# Revit family: Backflow_Preventer-DCDA-Zurn_Wilkins-Model_450DABG-(8-10_Inch)
name_source: partatom
category: Pipe Accessories
units: mm (PartAtom-declared; Revit-internal decimal feet)

## family parameters
Always vertical = Yes
Cut with Voids When Loaded = No
OmniClass Number = 23.65.55.14.21
OmniClass Title = Non-Return Valves for Liquid Services
Part Type = Valve - Breaks Into
Round Connector Dimension = Use Radius
Shared = No
Work Plane-Based = No

## types (2) — shared parameters
Assembly Code = D2020300
Bend Radius = 1"
Bend Radius Outside = 2"
DIM A - Inlet center to outlet center = 29"
DIM D - Center to bypass end = 13"
Default Elevation = 0"
Description = Double Check Detector Assembly
Flow Rate (GPM) = 0 GPM
Hydrostatic Test Pressure = 350.00 psi
Length = 29"
Main Material = Paint - Zurn - Blue - Ductile Iron
Manufacturer = Zurn Water, LLC
Manufacturer Brand = Zurn Wilkins
Max Working Water Pressure = 175.00 psi
Max Working Water Temperature = 140 °F
Model = 450DABG
Modified Date = 07/17/2025
Overall Length = 29"
Pipe Size = 1 3/32"
Product Documentation Link = https://files.zurn.com
Product Installation Sheet URL = https://files.zurn.com
Product Page URL = https://www.zurn.com
Product data URL = https://www.bimobject.com
Repair Parts URL = https://files.zurn.com
URL = https://www.zurn.com

## per-type parameters (varying)
| type | Butterfly gate valve | DIM B - Overall height of the valve | DIM C - Center to gate valve stem top | Height | Main Body DA | Nominal Diameter | Nominal Radius | Overall Height | Pressure Loss at Rated Flow | Product Weight (lbs) | Rated Flow |
| 10-450DABG (10" 450DABG) | Shut_Off_Valve-Butterfly-Zurn_Wilkins-Model_49G_Grooved-(8-10)_Inch : 10-49G (10" 49G) | 44 7/16" | 13" | 47 1/2" | Main Body 450 DA : 10" | 10" | 5" | 47 1/2" | 9.20 psi | 636 | 2300 GPM |
| 8-450DABG (8" 450DABG) | Shut_Off_Valve-Butterfly-Zurn_Wilkins-Model_49G_Grooved-(8-10)_Inch : 8-49G (8" 49G) | 42 9/16" | 12" | 46" | Main Body 450 DA : 8" | 8" | 4" | 46" | 8.10 psi | 546 | 1600 GPM |

## geometry (parser evidence)
native form markers: Sweep x14
no freeform markers — native parametric forms only
